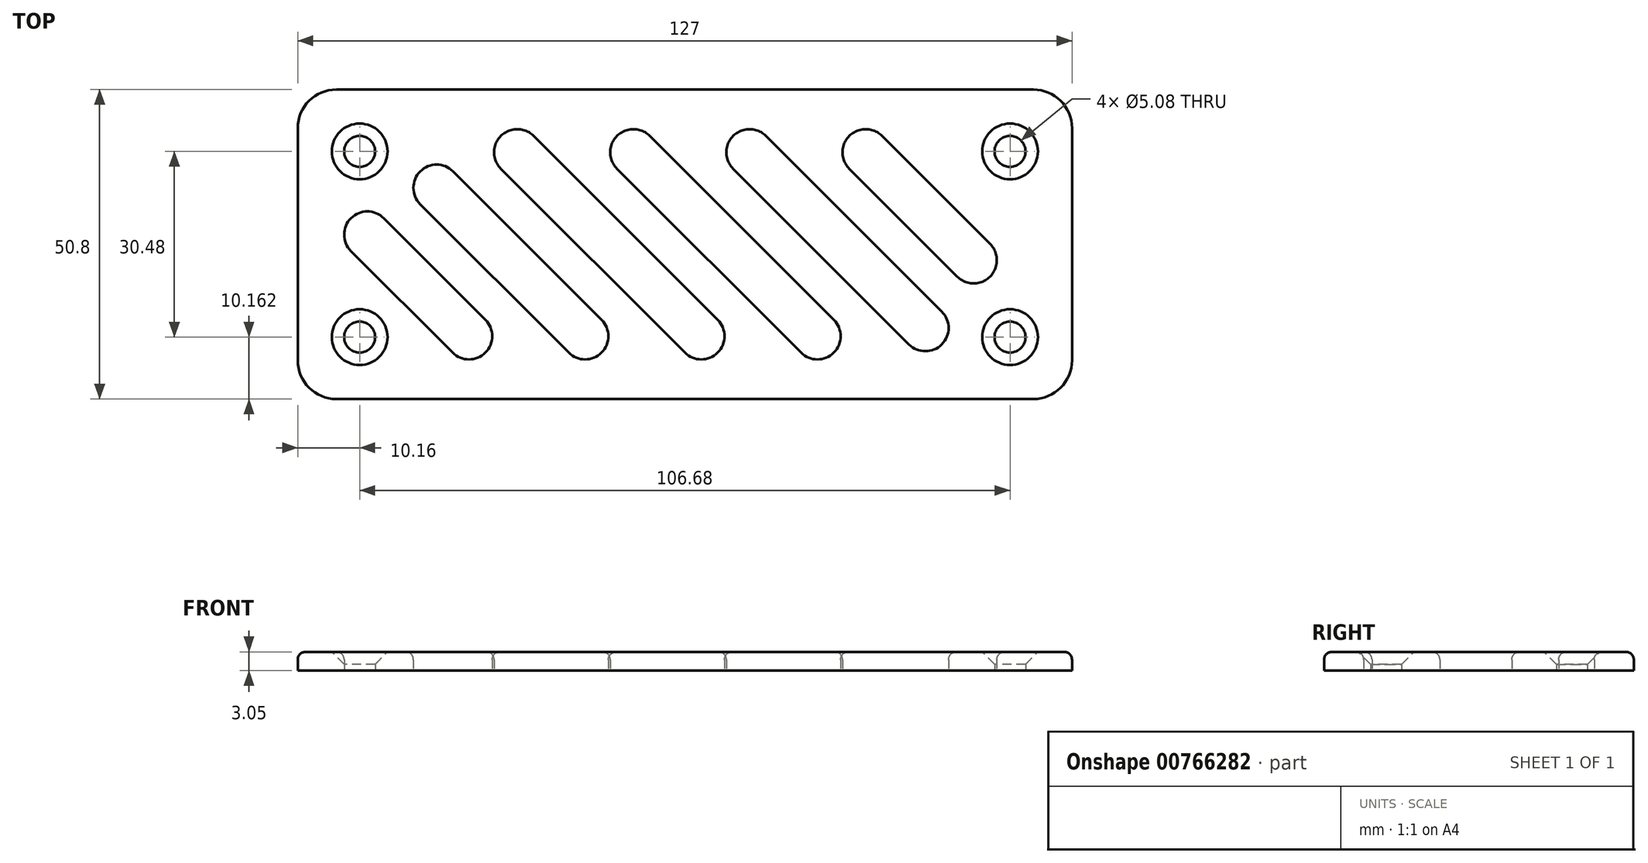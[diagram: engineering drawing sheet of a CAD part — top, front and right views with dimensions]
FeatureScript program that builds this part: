
annotation { "Feature Type Name" : "Feature", "Feature Type Description" : "" }
export const myFeature = defineFeature(function(context is Context, id is Id, definition is map)
    precondition{}
    {
        {
            var Q0;
            Q0=qCreatedBy(makeId("Top.planeOp"),FACE);
            var sketch = newSketch(context, id + "F0", { "sketchPlane" : qUnion([Q0])});
            skLineSegment(sketch, "E0.bottom", {"start": v(-76.2, 29.32) * mm, "end": v(38.1, 29.32) * mm});
            skLineSegment(sketch, "E0.top", {"start": v(-76.2, -21.48) * mm, "end": v(38.1, -21.48) * mm});
            skLineSegment(sketch, "E0.left", {"start": v(-82.55, 22.97) * mm, "end": v(-82.55, -15.13) * mm});
            skLineSegment(sketch, "E0.right", {"start": v(44.45, 22.97) * mm, "end": v(44.45, -15.13) * mm});
            skCircle(sketch, "E1", {"center": v(-72.39, 19.16) * mm, "radius": 2.54 * mm});
            skLineSegment(sketch, "E2", {"start": v(-82.55, 3.92) * mm, "end": v(-31.43, 3.92) * mm, "construction": true});
            skLineSegment(sketch, "E3", {"start": v(-19.05, 29.32) * mm, "end": v(-19.05, -49.96) * mm, "construction": true});
            skCircle(sketch, "E4.MirrorC", {"center": v(34.3, 19.16) * mm, "radius": 2.54 * mm});
            skCircle(sketch, "E5.MirrorC", {"center": v(-72.39, -11.32) * mm, "radius": 2.54 * mm});
            skCircle(sketch, "E6.MirrorC", {"center": v(34.3, -11.32) * mm, "radius": 2.54 * mm});
            skLineSegment(sketch, "E7", {"start": v(-5.73, 21.7) * mm, "end": v(23.1, -7.13) * mm});
            skLineSegment(sketch, "E8", {"start": v(-11.12, 16.31) * mm, "end": v(17.7, -12.51) * mm});
            skArc(sketch, "E9", {"start": v(-5.73, 21.7) * mm, "mid": v(-11.12, 21.7) * mm, "end": v(-11.12, 16.31) * mm});
            skArc(sketch, "E10", {"start": v(17.7, -12.51) * mm, "mid": v(23.1, -12.51) * mm, "end": v(23.1, -7.13) * mm});
            skLineSegment(sketch, "E11", {"start": v(17.7, -12.51) * mm, "end": v(30.97, 0.75) * mm, "construction": true});
            skLineSegment(sketch, "E12", {"start": v(-5.73, 21.7) * mm, "end": v(-25.2, 2.24) * mm, "construction": true});
            skLineSegment(sketch, "E13", {"start": v(-24.78, 21.7) * mm, "end": v(5.39, -8.47) * mm});
            skLineSegment(sketch, "E14", {"start": v(-30.17, 16.31) * mm, "end": v(0, -13.86) * mm});
            skArc(sketch, "E15", {"start": v(-24.78, 21.7) * mm, "mid": v(-30.17, 21.7) * mm, "end": v(-30.17, 16.31) * mm});
            skArc(sketch, "E16", {"start": v(0, -13.86) * mm, "mid": v(5.39, -13.86) * mm, "end": v(5.39, -8.47) * mm});
            skLineSegment(sketch, "E17", {"start": v(-43.83, 21.7) * mm, "end": v(-13.66, -8.47) * mm});
            skLineSegment(sketch, "E18", {"start": v(-49.22, 16.31) * mm, "end": v(-19.05, -13.86) * mm});
            skArc(sketch, "E19", {"start": v(-43.83, 21.7) * mm, "mid": v(-49.22, 21.7) * mm, "end": v(-49.22, 16.31) * mm});
            skArc(sketch, "E20", {"start": v(-19.05, -13.86) * mm, "mid": v(-13.66, -13.86) * mm, "end": v(-13.66, -8.47) * mm});
            skLineSegment(sketch, "E21", {"start": v(-57.07, 15.88) * mm, "end": v(-32.71, -8.47) * mm});
            skLineSegment(sketch, "E22", {"start": v(-62.45, 10.5) * mm, "end": v(-38.1, -13.86) * mm});
            skArc(sketch, "E23", {"start": v(-57.07, 15.88) * mm, "mid": v(-62.45, 15.88) * mm, "end": v(-62.45, 10.5) * mm});
            skArc(sketch, "E24", {"start": v(-38.1, -13.86) * mm, "mid": v(-32.71, -13.86) * mm, "end": v(-32.71, -8.47) * mm});
            skLineSegment(sketch, "E25", {"start": v(13.32, 21.7) * mm, "end": v(31.01, 4) * mm});
            skLineSegment(sketch, "E26", {"start": v(7.93, 16.31) * mm, "end": v(25.62, -1.38) * mm});
            skArc(sketch, "E27", {"start": v(13.32, 21.7) * mm, "mid": v(7.93, 21.7) * mm, "end": v(7.93, 16.31) * mm});
            skArc(sketch, "E28", {"start": v(25.62, -1.38) * mm, "mid": v(31.01, -1.38) * mm, "end": v(31.01, 4) * mm});
            skLineSegment(sketch, "E29", {"start": v(-68.43, 8.2) * mm, "end": v(-51.76, -8.47) * mm});
            skLineSegment(sketch, "E30", {"start": v(-73.81, 2.8) * mm, "end": v(-57.15, -13.86) * mm});
            skArc(sketch, "E31", {"start": v(-68.43, 8.2) * mm, "mid": v(-73.81, 8.2) * mm, "end": v(-73.81, 2.8) * mm});
            skArc(sketch, "E32", {"start": v(-57.15, -13.86) * mm, "mid": v(-51.76, -13.86) * mm, "end": v(-51.76, -8.47) * mm});
            skLineSegment(sketch, "E33", {"start": v(-57.07, 15.88) * mm, "end": v(-71.57, 1.38) * mm, "construction": true});
            skLineSegment(sketch, "E34", {"start": v(-68.43, 8.2) * mm, "end": v(-92.52, -15.9) * mm, "construction": true});
            skLineSegment(sketch, "E35", {"start": v(-40.5, 2.8) * mm, "end": v(-57.15, -13.86) * mm, "construction": true});
            skLineSegment(sketch, "E36", {"start": v(13.32, 21.7) * mm, "end": v(-5.97, 2.42) * mm, "construction": true});
            skLineSegment(sketch, "E37", {"start": v(-24.78, 21.7) * mm, "end": v(-50.31, -3.83) * mm, "construction": true});
            skLineSegment(sketch, "E38", {"start": v(-43.83, 21.7) * mm, "end": v(-53.36, 12.18) * mm, "construction": true});
            skLineSegment(sketch, "E39", {"start": v(-21.44, 2.8) * mm, "end": v(-38.1, -13.86) * mm, "construction": true});
            skLineSegment(sketch, "E40", {"start": v(-2.4, 2.8) * mm, "end": v(-19.05, -13.86) * mm, "construction": true});
            skLineSegment(sketch, "E41", {"start": v(10.6, -3.26) * mm, "end": v(0, -13.86) * mm, "construction": true});
            skLineSegment(sketch, "E42", {"start": v(55.31, 28.3) * mm, "end": v(25.62, -1.38) * mm, "construction": true});
            skPoint(sketch, "E43.visualSharp", {"position": v(44.45, 29.32) * mm});
            skArc(sketch, "E43.filletArc", {"start": v(44.45, 22.97) * mm, "mid": v(42.6, 27.46) * mm, "end": v(38.1, 29.32) * mm});
            skPoint(sketch, "E44.visualSharp", {"position": v(44.45, -21.48) * mm});
            skArc(sketch, "E44.filletArc", {"start": v(38.1, -21.48) * mm, "mid": v(42.6, -19.62) * mm, "end": v(44.45, -15.13) * mm});
            skPoint(sketch, "E45.visualSharp", {"position": v(-82.55, 29.32) * mm});
            skArc(sketch, "E45.filletArc", {"start": v(-76.2, 29.32) * mm, "mid": v(-80.7, 27.46) * mm, "end": v(-82.55, 22.97) * mm});
            skPoint(sketch, "E46.visualSharp", {"position": v(-82.55, -21.48) * mm});
            skArc(sketch, "E46.filletArc", {"start": v(-82.55, -15.13) * mm, "mid": v(-80.7, -19.62) * mm, "end": v(-76.2, -21.48) * mm});
            skSolve(sketch);
        }
        {
            var Q0;
            Q0=makeQuery(id+"F0.imprint","IMPRINT",FACE,{"disambiguationData":[TD([[makeQuery(id+"F0.imprint","IMPRINT",EDGE,{"derivedFrom":sQuery(id+"F0.wireOp",EDGE,"E0.bottom")}),-1.0]])]});
            extrude(context, id + "F1", {"entities" : qUnion([Q0]), "depth" : 3.05 * mm, "offsetDistance" : 25.4 * mm});
        }
        {
            var Q0;
            Q0=makeQuery(id+"F1.opExtrude","CAP_EDGE",EDGE,{"disambiguationData":[OSD([sQuery(id+"F0.wireOp",EDGE,"E4.MirrorC")])],"isStart":false});
            var Q1;
            Q1=makeQuery(id+"F1.opExtrude","CAP_EDGE",EDGE,{"disambiguationData":[OSD([sQuery(id+"F0.wireOp",EDGE,"E6.MirrorC")])],"isStart":false});
            var Q2;
            Q2=makeQuery(id+"F1.opExtrude","CAP_EDGE",EDGE,{"disambiguationData":[OSD([sQuery(id+"F0.wireOp",EDGE,"E1")])],"isStart":false});
            var Q3;
            Q3=makeQuery(id+"F1.opExtrude","CAP_EDGE",EDGE,{"disambiguationData":[OSD([sQuery(id+"F0.wireOp",EDGE,"E5.MirrorC")])],"isStart":false});
            chamfer(context, id + "F2", {"entities" : qUnion([Q0, Q1, Q2, Q3]), "width" : 2.03 * mm, "tangentPropagation" : true});
        }
        {
            var Q0;
            Q0=makeQuery(id+"F1.opExtrude","CAP_EDGE",EDGE,{"disambiguationData":[OSD([sQuery(id+"F0.wireOp",EDGE,"E0.bottom")])],"isStart":false});
            var Q1;
            Q1=makeQuery(id+"F1.opExtrude","CAP_EDGE",EDGE,{"disambiguationData":[OSD([sQuery(id+"F0.wireOp",EDGE,"E17")])],"isStart":false});
            var Q2;
            Q2=makeQuery(id+"F1.opExtrude","CAP_EDGE",EDGE,{"disambiguationData":[OSD([sQuery(id+"F0.wireOp",EDGE,"E13")])],"isStart":false});
            var Q3;
            Q3=makeQuery(id+"F1.opExtrude","CAP_EDGE",EDGE,{"disambiguationData":[OSD([sQuery(id+"F0.wireOp",EDGE,"E8")])],"isStart":false});
            var Q4;
            Q4=makeQuery(id+"F1.opExtrude","CAP_EDGE",EDGE,{"disambiguationData":[OSD([sQuery(id+"F0.wireOp",EDGE,"E26")])],"isStart":false});
            var Q5;
            Q5=makeQuery(id+"F1.opExtrude","CAP_EDGE",EDGE,{"disambiguationData":[OSD([sQuery(id+"F0.wireOp",EDGE,"E22")])],"isStart":false});
            var Q6;
            Q6=makeQuery(id+"F1.opExtrude","CAP_EDGE",EDGE,{"disambiguationData":[OSD([sQuery(id+"F0.wireOp",EDGE,"E30")])],"isStart":false});
            fillet(context, id + "F3", {"entities" : qUnion([Q0, Q1, Q2, Q3, Q4, Q5, Q6]), "radius" : 1.27 * mm, "tangentPropagation" : true, "allowEdgeOverflow" : false});
        }
    });
